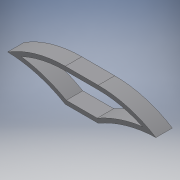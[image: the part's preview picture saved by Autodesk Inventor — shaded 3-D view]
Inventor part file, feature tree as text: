
AUTODESK INVENTOR PART (.ipt)
format: ipt  version: 2016 SP2 (Build 200236200, 236)  size: 112,128 bytes
history: native  units: mm
features: extrude x1, sketch x1
ambient origin geometry x8: Origin, YZ Plane, XZ Plane, XY Plane, X Axis, Y Axis, Z Axis, Center Point
bodies: Volumenkörper1 (feature_tree)
feature tree (2):
  extrude  "Extrusion1"  Depth=5.0mm
  sketch  "Skizze1"  dims[d0=5.0mm d1=22.5mm d2=5.0mm d3=5.0mm d4=5.0mm d6=1.2mm d7=10.0mm d8=5.0mm d9=0.0mm]
